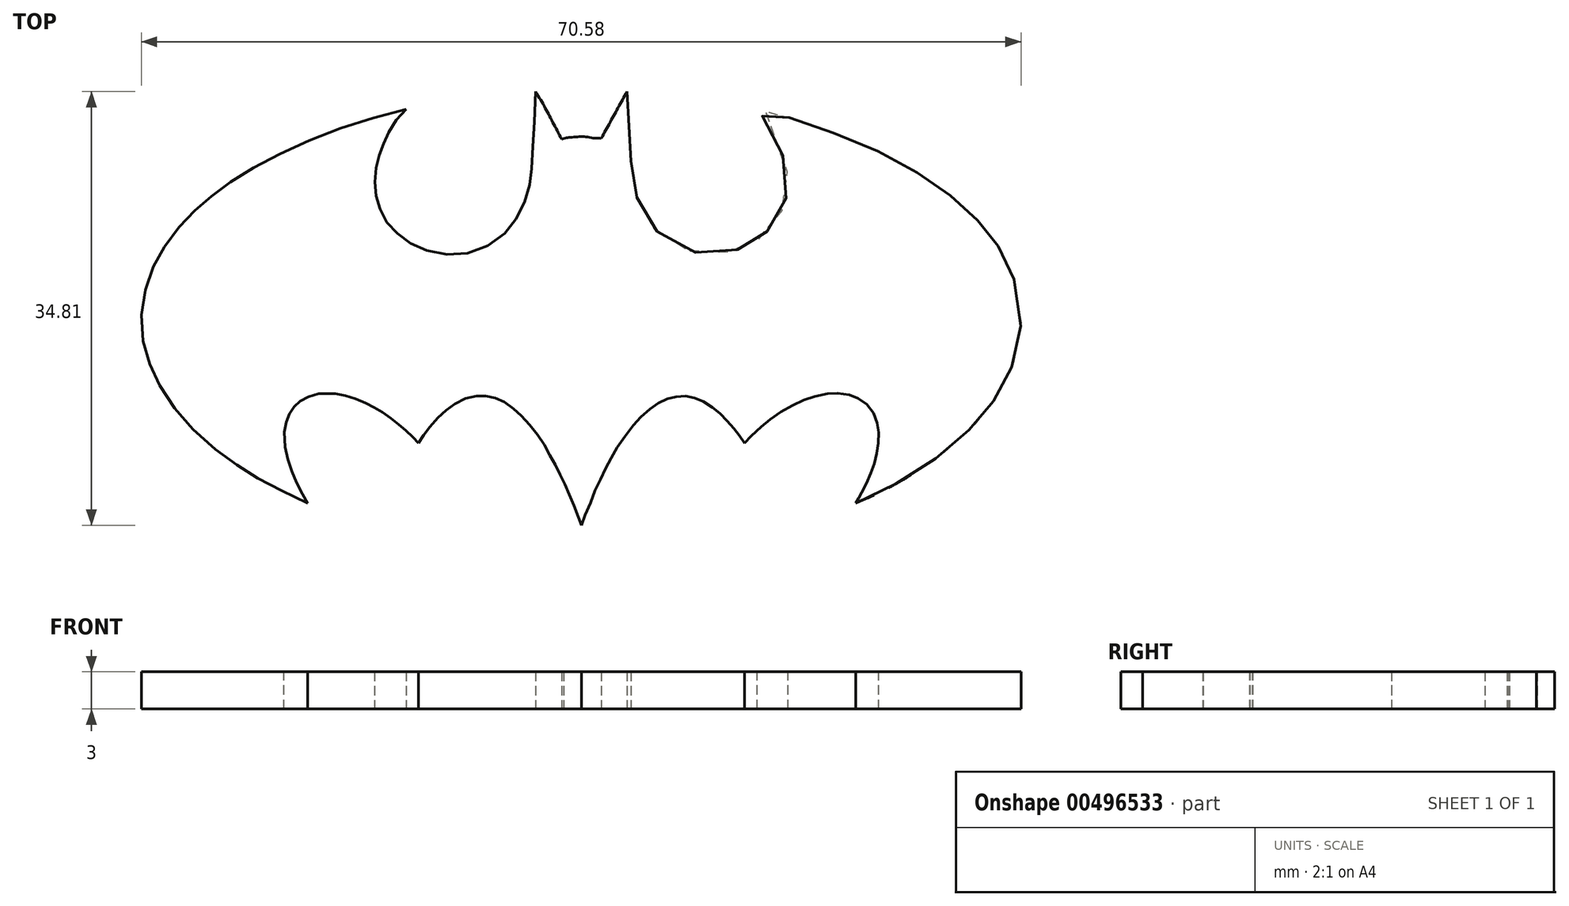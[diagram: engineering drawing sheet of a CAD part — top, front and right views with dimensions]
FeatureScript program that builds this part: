
annotation { "Feature Type Name" : "Feature", "Feature Type Description" : "" }
export const myFeature = defineFeature(function(context is Context, id is Id, definition is map)
    precondition{}
    {
        {
            var Q0;
            Q0=qCreatedBy(makeId("Top.planeOp"),FACE);
            var sketch = newSketch(context, id + "F0", { "sketchPlane" : qUnion([Q0])});
            skFitSpline(sketch, "E0", {"points": [v(43.89, 42.95) * mm, v(41.82, 39.2) * mm], "startDerivative": vector(-2.06, -3.78) * mm, "endDerivative": vector(-2.06, -3.78) * mm});
            skFitSpline(sketch, "E1", {"points": [v(43.89, 42.95) * mm, v(44.2, 37.38) * mm], "startDerivative": vector(0.3, -5.69) * mm, "endDerivative": vector(0.3, -5.69) * mm});
            skFitSpline(sketch, "E2", {"points": [v(44.2, 37.38) * mm, v(44.21, 36.96) * mm, v(44.24, 36.55) * mm, v(44.28, 36.32) * mm, v(44.32, 36.04) * mm, v(44.36, 35.79) * mm, v(44.4, 35.54) * mm, v(44.44, 35.34) * mm, v(44.49, 35.12) * mm, v(44.57, 34.82) * mm, v(44.64, 34.56) * mm, v(44.74, 34.27) * mm, v(44.9, 33.88) * mm, v(45.02, 33.56) * mm, v(45.15, 33.31) * mm, v(45.34, 32.98) * mm, v(45.5, 32.73) * mm, v(45.7, 32.41) * mm, v(45.88, 32.2) * mm, v(46.06, 31.97) * mm, v(46.27, 31.76) * mm, v(46.6, 31.46) * mm, v(46.97, 31.15) * mm, v(47.32, 30.9) * mm, v(47.67, 30.7) * mm, v(48.04, 30.5) * mm, v(48.46, 30.32) * mm, v(48.83, 30.19) * mm, v(49.12, 30.11) * mm, v(49.44, 30.05) * mm, v(49.72, 29.98) * mm, v(50.04, 29.95) * mm, v(50.26, 29.93) * mm, v(51.25, 29.93) * mm, v(51.44, 29.96) * mm, v(51.69, 30.02) * mm, v(52.04, 30.08) * mm, v(52.33, 30.16) * mm, v(52.6, 30.21) * mm, v(52.9, 30.32) * mm, v(53.2, 30.45) * mm, v(53.5, 30.6) * mm, v(53.68, 30.67) * mm, v(53.85, 30.76) * mm, v(54.03, 30.86) * mm, v(54.2, 30.96) * mm, v(54.4, 31.1) * mm, v(54.58, 31.23) * mm, v(54.8, 31.4) * mm, v(55, 31.6) * mm, v(55.28, 31.85) * mm, v(55.58, 32.2) * mm, v(55.8, 32.44) * mm, v(55.91, 32.63) * mm, v(56.1, 32.94) * mm, v(56.22, 33.17) * mm, v(56.32, 33.4) * mm, v(56.4, 33.6) * mm, v(56.5, 33.84) * mm, v(56.6, 34.19) * mm, v(56.67, 34.5) * mm, v(56.74, 34.8) * mm, v(56.78, 35.24) * mm, v(56.83, 35.76) * mm, v(56.8, 36.27) * mm, v(56.73, 36.63) * mm, v(56.68, 36.9) * mm, v(56.57, 37.32) * mm, v(56.45, 37.7) * mm, v(56.36, 38.02) * mm, v(56.18, 38.47) * mm, v(56, 38.92) * mm, v(55.8, 39.32) * mm, v(55.62, 39.66) * mm, v(55.39, 40.03) * mm, v(55.18, 40.39) * mm, v(54.96, 40.7) * mm, v(54.76, 40.97) * mm, v(54.6, 41.19) * mm, v(54.42, 41.42) * mm, v(54.35, 41.5) * mm, v(54.5, 41.5) * mm, v(54.8, 41.42) * mm, v(55.15, 41.34) * mm, v(55.58, 41.21) * mm, v(55.9, 41.13) * mm, v(56.37, 41) * mm, v(56.95, 40.84) * mm, v(57.43, 40.7) * mm, v(57.9, 40.53) * mm, v(58.29, 40.42) * mm, v(58.69, 40.28) * mm, v(59.14, 40.13) * mm, v(59.59, 39.96) * mm, v(59.93, 39.83) * mm, v(60.4, 39.66) * mm, v(60.8, 39.53) * mm, v(61.22, 39.35) * mm, v(61.73, 39.16) * mm, v(62.18, 38.98) * mm, v(62.7, 38.75) * mm, v(63.19, 38.54) * mm, v(63.62, 38.34) * mm, v(63.94, 38.2) * mm, v(64.26, 38.03) * mm, v(64.8, 37.78) * mm, v(65.05, 37.67) * mm, v(65.2, 37.58) * mm, v(65.55, 37.38) * mm, v(65.99, 37.17) * mm, v(66.53, 36.86) * mm, v(66.88, 36.64) * mm, v(67.13, 36.48) * mm, v(67.38, 36.33) * mm, v(67.64, 36.16) * mm, v(67.92, 35.98) * mm, v(68.17, 35.82) * mm, v(68.44, 35.63) * mm, v(68.73, 35.44) * mm, v(69.03, 35.2) * mm, v(69.4, 34.95) * mm, v(69.65, 34.76) * mm, v(69.9, 34.56) * mm, v(70.1, 34.4) * mm, v(70.36, 34.2) * mm, v(70.6, 33.99) * mm, v(70.8, 33.8) * mm, v(71.03, 33.59) * mm, v(71.25, 33.38) * mm, v(71.45, 33.17) * mm, v(71.62, 33.01) * mm, v(71.82, 32.8) * mm, v(72, 32.62) * mm, v(72.23, 32.38) * mm, v(72.42, 32.18) * mm, v(72.56, 32) * mm, v(72.68, 31.86) * mm, v(72.82, 31.68) * mm, v(72.97, 31.5) * mm, v(73.1, 31.33) * mm, v(73.2, 31.2) * mm, v(73.31, 31.03) * mm, v(73.44, 30.85) * mm, v(73.54, 30.7) * mm, v(73.7, 30.47) * mm, v(73.83, 30.26) * mm, v(73.96, 30.05) * mm, v(74.07, 29.86) * mm, v(74.22, 29.58) * mm, v(74.38, 29.26) * mm, v(74.5, 29) * mm, v(74.64, 28.71) * mm, v(74.7, 28.5) * mm, v(74.81, 28.27) * mm, v(74.94, 27.93) * mm, v(75.01, 27.66) * mm, v(75.11, 27.33) * mm, v(75.19, 27.12) * mm, v(75.27, 26.75) * mm, v(75.35, 26.34) * mm, v(75.42, 25.8) * mm, v(75.47, 25.32) * mm, v(75.5, 24.6) * mm, v(75.48, 23.85) * mm, v(75.45, 23.43) * mm, v(75.4, 23.14) * mm, v(75.34, 22.8) * mm, v(75.25, 22.44) * mm, v(75.17, 22.12) * mm, v(75.07, 21.78) * mm, v(74.97, 21.43) * mm, v(74.84, 21.09) * mm, v(74.73, 20.76) * mm, v(74.63, 20.53) * mm, v(74.52, 20.29) * mm, v(74.4, 20.07) * mm, v(74.29, 19.75) * mm, v(74.12, 19.44) * mm, v(73.96, 19.16) * mm, v(73.83, 18.94) * mm, v(73.6, 18.56) * mm, v(73.4, 18.28) * mm, v(73.23, 18.01) * mm, v(72.93, 17.61) * mm, v(72.75, 17.39) * mm, v(72.57, 17.15) * mm, v(72.39, 16.94) * mm, v(72.2, 16.71) * mm, v(72.08, 16.59) * mm, v(71.96, 16.43) * mm, v(71.79, 16.25) * mm, v(71.6, 16.07) * mm, v(71.36, 15.81) * mm, v(70.83, 15.29) * mm, v(70.52, 15) * mm, v(70.24, 14.75) * mm, v(69.97, 14.52) * mm, v(69.69, 14.28) * mm, v(69.44, 14.09) * mm, v(69.21, 13.91) * mm, v(68.9, 13.68) * mm, v(68.63, 13.48) * mm, v(68.39, 13.3) * mm, v(68.16, 13.15) * mm, v(67.84, 12.91) * mm, v(67.4, 12.62) * mm, v(66.97, 12.35) * mm, v(66.6, 12.15) * mm, v(66.2, 11.88) * mm, v(65.6, 11.55) * mm, v(65.07, 11.24) * mm, v(64.63, 11.01) * mm, v(64.21, 10.8) * mm, v(63.82, 10.61) * mm, v(63.4, 10.41) * mm, v(63.08, 10.28) * mm, v(62.75, 10.14) * mm, v(62.5, 10.03) * mm, v(62.24, 9.92) * mm], "startDerivative": vector(2.99, -66.58) * mm, "endDerivative": vector(-65, -27.08) * mm});
            skFitSpline(sketch, "E3", {"points": [v(62.24, 9.92) * mm, v(62.3, 10.01) * mm, v(62.38, 10.18) * mm, v(62.5, 10.4) * mm, v(62.62, 10.62) * mm, v(62.78, 10.93) * mm, v(63.08, 11.48) * mm, v(63.39, 12.19) * mm, v(63.6, 12.71) * mm, v(63.8, 13.34) * mm, v(63.93, 13.97) * mm, v(64.04, 14.57) * mm, v(64.08, 15.22) * mm, v(64.05, 15.9) * mm, v(63.94, 16.4) * mm, v(63.77, 16.94) * mm, v(63.39, 17.6) * mm, v(62.89, 18.05) * mm, v(62.37, 18.35) * mm, v(61.95, 18.54) * mm, v(61.13, 18.73) * mm, v(60.5, 18.74) * mm, v(59.86, 18.7) * mm, v(58.92, 18.46) * mm, v(58.2, 18.23) * mm, v(57.37, 17.86) * mm, v(56.48, 17.38) * mm, v(55.62, 16.82) * mm, v(54.95, 16.3) * mm, v(54.32, 15.74) * mm, v(53.55, 15.03) * mm, v(53.3, 14.75) * mm], "startDerivative": vector(4.3, 6.34) * mm, "endDerivative": vector(-10.38, -10.24) * mm});
            skFitSpline(sketch, "E4", {"points": [v(53.3, 14.75) * mm, v(53.1, 15.04) * mm, v(52.85, 15.41) * mm, v(52.62, 15.71) * mm, v(52.34, 16.06) * mm, v(52.02, 16.43) * mm, v(51.68, 16.79) * mm, v(51.32, 17.14) * mm, v(51.03, 17.38) * mm, v(50.52, 17.75) * mm, v(50.08, 18.03) * mm, v(49.68, 18.24) * mm, v(49.25, 18.38) * mm, v(48.88, 18.47) * mm, v(48.39, 18.52) * mm, v(47.95, 18.48) * mm, v(47.55, 18.4) * mm, v(47.18, 18.31) * mm, v(46.77, 18.14) * mm, v(46.3, 17.88) * mm, v(45.88, 17.6) * mm, v(45.4, 17.21) * mm, v(44.87, 16.7) * mm, v(44.45, 16.24) * mm, v(43.97, 15.63) * mm, v(43.35, 14.75) * mm, v(42.95, 14.14) * mm, v(42.57, 13.47) * mm, v(42.26, 12.89) * mm, v(42.03, 12.36) * mm, v(41.64, 11.6) * mm, v(41.3, 10.9) * mm, v(41.03, 10.14) * mm, v(40.68, 9.3) * mm, v(40.41, 8.64) * mm, v(40.24, 8.14) * mm], "startDerivative": vector(-8.42, 12.55) * mm, "endDerivative": vector(-6.02, -17.5) * mm});
            skFitSpline(sketch, "E5", {"points": [v(40.24, 8.14) * mm, v(40.16, 8.3) * mm, v(40.1, 8.54) * mm, v(40, 8.76) * mm, v(39.86, 9.15) * mm, v(39.7, 9.57) * mm, v(39.54, 9.94) * mm, v(39.39, 10.26) * mm, v(39.22, 10.67) * mm, v(39.1, 11) * mm, v(38.95, 11.33) * mm, v(38.8, 11.63) * mm, v(38.67, 11.95) * mm, v(38.52, 12.24) * mm, v(38.36, 12.54) * mm, v(38.2, 12.89) * mm, v(38.06, 13.15) * mm, v(37.92, 13.44) * mm, v(37.7, 13.77) * mm, v(37.57, 14.1) * mm, v(37.31, 14.5) * mm, v(37.13, 14.8) * mm, v(36.9, 15.14) * mm, v(36.64, 15.5) * mm, v(36.39, 15.86) * mm, v(36.08, 16.2) * mm, v(35.85, 16.46) * mm, v(35.5, 16.85) * mm, v(35.22, 17.12) * mm, v(34.99, 17.33) * mm, v(34.73, 17.55) * mm, v(34.46, 17.77) * mm, v(34.14, 17.98) * mm, v(33.9, 18.11) * mm, v(33.64, 18.24) * mm, v(33.33, 18.35) * mm, v(33.05, 18.43) * mm, v(32.75, 18.49) * mm, v(32.55, 18.5) * mm, v(32.3, 18.52) * mm, v(32.05, 18.53) * mm, v(31.81, 18.53) * mm, v(31.6, 18.5) * mm, v(31.16, 18.4) * mm, v(30.73, 18.23) * mm, v(30.35, 18.05) * mm, v(30.03, 17.85) * mm, v(29.83, 17.72) * mm, v(29.52, 17.5) * mm, v(29.25, 17.26) * mm, v(28.96, 17) * mm, v(28.73, 16.77) * mm, v(28.47, 16.5) * mm, v(28.15, 16.14) * mm, v(27.94, 15.9) * mm, v(27.77, 15.66) * mm, v(27.6, 15.4) * mm, v(27.45, 15.2) * mm, v(27.27, 14.92) * mm, v(27.16, 14.74) * mm], "startDerivative": vector(-6.71, 12.16) * mm, "endDerivative": vector(-9.07, -11.86) * mm});
            skFitSpline(sketch, "E6", {"points": [v(27.16, 14.74) * mm, v(27.12, 14.8) * mm, v(27.06, 14.86) * mm, v(26.93, 15) * mm, v(26.82, 15.11) * mm, v(26.65, 15.28) * mm, v(26.51, 15.41) * mm, v(26.38, 15.54) * mm, v(26.23, 15.69) * mm, v(26.08, 15.8) * mm, v(25.92, 15.95) * mm, v(25.78, 16.06) * mm, v(25.64, 16.2) * mm, v(25.48, 16.32) * mm, v(25.29, 16.46) * mm, v(25.1, 16.62) * mm, v(24.95, 16.73) * mm, v(24.78, 16.85) * mm, v(24.6, 16.98) * mm, v(24.41, 17.1) * mm, v(24.22, 17.24) * mm, v(24.02, 17.36) * mm, v(23.86, 17.45) * mm, v(23.72, 17.54) * mm, v(23.53, 17.64) * mm, v(23.39, 17.73) * mm, v(23.24, 17.8) * mm, v(23.03, 17.9) * mm, v(22.72, 18.04) * mm, v(22.44, 18.18) * mm, v(22.22, 18.26) * mm, v(22.04, 18.33) * mm, v(21.8, 18.4) * mm, v(21.6, 18.47) * mm, v(21.31, 18.54) * mm, v(21.08, 18.6) * mm, v(20.83, 18.65) * mm, v(20.7, 18.68) * mm, v(20.46, 18.72) * mm, v(20.21, 18.74) * mm, v(19.26, 18.71) * mm, v(18.96, 18.66) * mm, v(18.74, 18.6) * mm, v(18.46, 18.51) * mm, v(18.29, 18.45) * mm, v(18.1, 18.36) * mm, v(17.95, 18.28) * mm, v(17.83, 18.21) * mm, v(17.64, 18.08) * mm, v(17.53, 18) * mm, v(17.4, 17.88) * mm, v(17.3, 17.8) * mm, v(17.2, 17.68) * mm, v(17.14, 17.6) * mm, v(17.03, 17.45) * mm, v(16.92, 17.32) * mm, v(16.84, 17.15) * mm, v(16.76, 17.03) * mm, v(16.69, 16.85) * mm, v(16.6, 16.65) * mm, v(16.56, 16.5) * mm, v(16.53, 16.34) * mm, v(16.48, 16.19) * mm, v(16.45, 16.01) * mm, v(16.42, 15.7) * mm, v(16.38, 15.39) * mm, v(16.42, 14.8) * mm, v(16.48, 14.31) * mm, v(16.52, 14.06) * mm, v(16.6, 13.75) * mm, v(16.71, 13.3) * mm, v(16.82, 12.98) * mm, v(16.93, 12.65) * mm, v(17.02, 12.38) * mm, v(17.15, 12.06) * mm, v(17.3, 11.76) * mm, v(17.44, 11.46) * mm, v(17.61, 11.13) * mm, v(17.78, 10.82) * mm, v(17.9, 10.53) * mm, v(18.04, 10.32) * mm, v(18.14, 10.13) * mm, v(18.26, 9.92) * mm], "startDerivative": vector(-5.5, 8.38) * mm, "endDerivative": vector(10.2, -17.2) * mm});
            skFitSpline(sketch, "E7", {"points": [v(41.82, 39.2) * mm, v(41.22, 39.22) * mm, v(40.49, 39.34) * mm, v(39.83, 39.31) * mm, v(39.2, 39.27) * mm, v(38.82, 39.2) * mm], "startDerivative": vector(-3.01, 0.62) * mm, "endDerivative": vector(-2.77, -0.41) * mm});
            skFitSpline(sketch, "E8", {"points": [v(38.82, 39.2) * mm, v(38.66, 39.13) * mm], "startDerivative": vector(-0.12, -0.06) * mm, "endDerivative": vector(-0.12, -0.06) * mm});
            skFitSpline(sketch, "E9", {"points": [v(38.66, 39.13) * mm, v(37.95, 40.46) * mm, v(37.3, 41.7) * mm, v(36.55, 42.95) * mm], "startDerivative": vector(-2.15, 3.94) * mm, "endDerivative": vector(-2.33, 3.76) * mm});
            skFitSpline(sketch, "E10", {"points": [v(36.55, 42.95) * mm, v(36.45, 40.46) * mm, v(36.36, 38.74) * mm, v(36.26, 37.27) * mm, v(36.2, 36.3) * mm, v(36.1, 35.66) * mm, v(35.92, 34.8) * mm, v(35.6, 33.9) * mm, v(35.2, 33.05) * mm, v(34.56, 32.09) * mm, v(34.04, 31.53) * mm, v(33.04, 30.77) * mm, v(32.03, 30.3) * mm, v(30.7, 29.9) * mm, v(29.59, 29.88) * mm, v(28.52, 30) * mm, v(27.31, 30.38) * mm, v(26.62, 30.71) * mm, v(25.9, 31.17) * mm, v(25.46, 31.58) * mm, v(24.95, 32.07) * mm, v(24.58, 32.56) * mm, v(24.27, 33.09) * mm, v(24, 33.71) * mm, v(23.84, 34.24) * mm, v(23.75, 34.63) * mm, v(23.67, 35.15) * mm, v(23.65, 35.7) * mm, v(23.7, 36.4) * mm, v(23.76, 36.82) * mm, v(23.84, 37.26) * mm, v(23.97, 37.75) * mm, v(24.12, 38.19) * mm, v(24.28, 38.6) * mm, v(24.4, 38.88) * mm, v(24.53, 39.22) * mm, v(24.77, 39.7) * mm, v(25.06, 40.22) * mm, v(25.4, 40.66) * mm, v(25.7, 41.05) * mm, v(26.18, 41.54) * mm], "startDerivative": vector(-2.5, -58.12) * mm, "endDerivative": vector(17.97, 22.26) * mm});
            skFitSpline(sketch, "E11", {"points": [v(26.18, 41.54) * mm, v(25.3, 41.37) * mm, v(23.92, 40.97) * mm, v(22.63, 40.55) * mm, v(21.55, 40.22) * mm, v(20.18, 39.72) * mm, v(19.13, 39.32) * mm, v(18.13, 38.94) * mm, v(17.03, 38.44) * mm, v(16.14, 38.01) * mm, v(15.23, 37.56) * mm, v(14.47, 37.16) * mm, v(13.7, 36.71) * mm, v(13.14, 36.38) * mm, v(12.45, 35.94) * mm, v(11.77, 35.47) * mm, v(11.2, 35.04) * mm, v(10.86, 34.8) * mm, v(10.42, 34.44) * mm, v(10.03, 34.12) * mm, v(9.72, 33.86) * mm, v(9.34, 33.52) * mm, v(8.95, 33.15) * mm, v(8.53, 32.7) * mm, v(8.15, 32.31) * mm, v(7.74, 31.84) * mm, v(7.33, 31.28) * mm, v(7, 30.8) * mm, v(6.65, 30.28) * mm, v(6.37, 29.81) * mm, v(6.15, 29.41) * mm, v(5.9, 28.9) * mm, v(5.69, 28.43) * mm, v(5.5, 27.88) * mm, v(5.27, 27.13) * mm, v(5.11, 26.46) * mm, v(5.03, 25.92) * mm, v(4.95, 25.18) * mm, v(4.92, 24.45) * mm, v(4.96, 23.73) * mm, v(5.05, 22.97) * mm, v(5.18, 22.35) * mm, v(5.35, 21.8) * mm, v(5.55, 21.28) * mm, v(5.82, 20.6) * mm, v(6.03, 20.1) * mm, v(6.24, 19.64) * mm, v(6.6, 19.04) * mm, v(7.02, 18.35) * mm, v(7.5, 17.67) * mm, v(7.9, 17.13) * mm, v(8.46, 16.5) * mm, v(9.04, 15.88) * mm, v(9.8, 15.18) * mm, v(10.52, 14.54) * mm, v(11.16, 14) * mm, v(11.78, 13.54) * mm, v(12.31, 13.16) * mm, v(12.93, 12.75) * mm, v(13.38, 12.45) * mm, v(13.96, 12.1) * mm, v(14.56, 11.76) * mm, v(15.25, 11.39) * mm, v(15.92, 11.05) * mm, v(16.63, 10.67) * mm, v(17.28, 10.35) * mm, v(18.26, 9.92) * mm], "startDerivative": vector(-49.9, -8.5) * mm, "endDerivative": vector(57.03, -24.7) * mm});
            skSolve(sketch);
        }
        {
            var Q0;
            Q0 = qSketchRegion(id + "F0", true);
            extrude(context, id + "F1", {"entities" : qUnion([Q0]), "depth" : 3 * mm, "offsetDistance" : 25 * mm});
        }
    });
